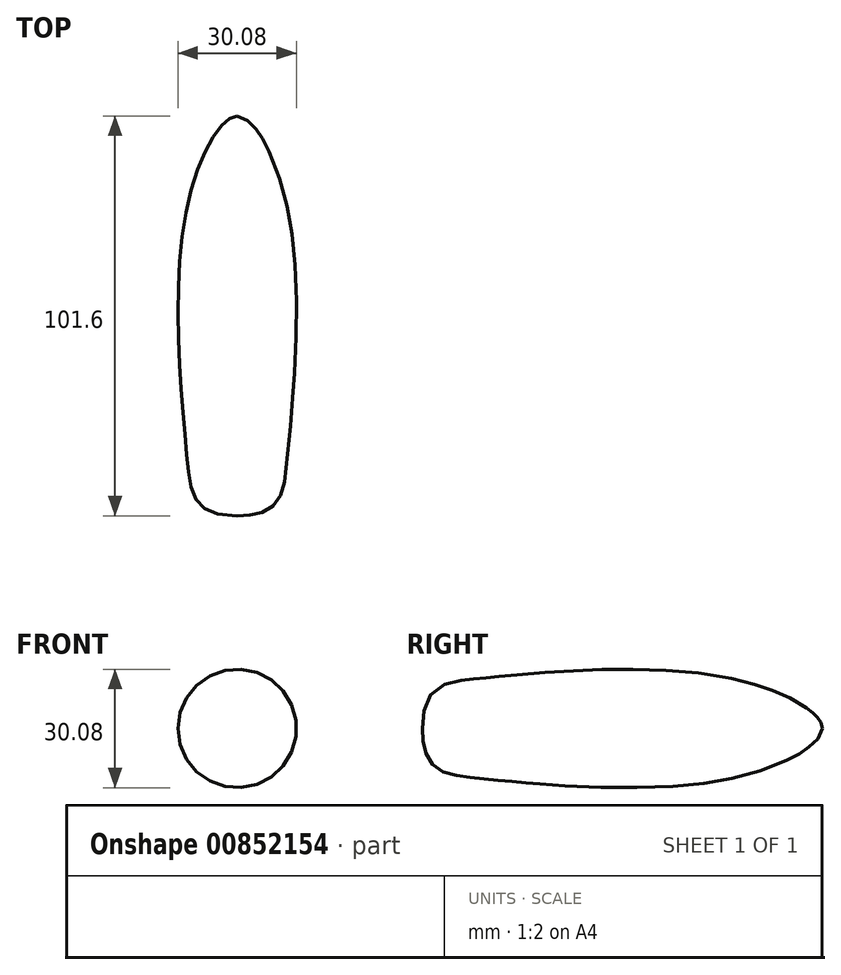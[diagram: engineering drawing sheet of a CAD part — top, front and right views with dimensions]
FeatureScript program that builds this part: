
annotation { "Feature Type Name" : "Feature", "Feature Type Description" : "" }
export const myFeature = defineFeature(function(context is Context, id is Id, definition is map)
    precondition{}
    {
        {
            var Q0;
            Q0=qCreatedBy(makeId("Top.planeOp"),FACE);
            var sketch = newSketch(context, id + "F0", { "sketchPlane" : qUnion([Q0])});
            skLineSegment(sketch, "E0", {"start": v(0, 0) * mm, "end": v(-12.7, 0) * mm, "construction": true});
            skLineSegment(sketch, "E1", {"start": v(-12.7, 0) * mm, "end": v(-12.7, 88.9) * mm, "construction": true});
            skLineSegment(sketch, "E2", {"start": v(0, 101.6) * mm, "end": v(0, 101.6) * mm});
            skLineSegment(sketch, "E3", {"start": v(0, 101.6) * mm, "end": v(0, 0) * mm, "construction": true});
            skPoint(sketch, "E4.visualSharp", {"position": v(-12.7, 101.6) * mm});
            skArc(sketch, "E4.filletArc", {"start": v(0, 101.6) * mm, "mid": v(-12.7, 88.9) * mm, "end": v(0, 76.2) * mm, "construction": true});
            skFitSpline(sketch, "E5", {"points": [v(0, 101.6) * mm, v(-12.7, 78.56) * mm, v(-12.7, 14.4) * mm, v(0, 0) * mm], "startDerivative": vector(-42.96, 0) * mm, "endDerivative": vector(135.67, 0) * mm});
            skLineSegment(sketch, "E6", {"start": v(0, 101.6) * mm, "end": v(-17.96, 101.6) * mm, "construction": true});
            skPoint(sketch, "E7", {"position": v(-12.7, 44.45) * mm});
            skSolve(sketch);
        }
        {
            var Q0;
            Q0=sQuery(id+"F0.wireOp",EDGE,"E5");
            var Q1;
            Q1=sQuery(id+"F0.wireOp",EDGE,"E3");
            revolve(context, id + "F1", {"bodyType" : ToolBodyType.SURFACE, "surfaceOperationType" : NewSurfaceOperationType.NEW, "surfaceEntities" : qUnion([Q0]), "axis" : qUnion([Q1]), "revolveType" : RevolveType.FULL});
        }
    });
